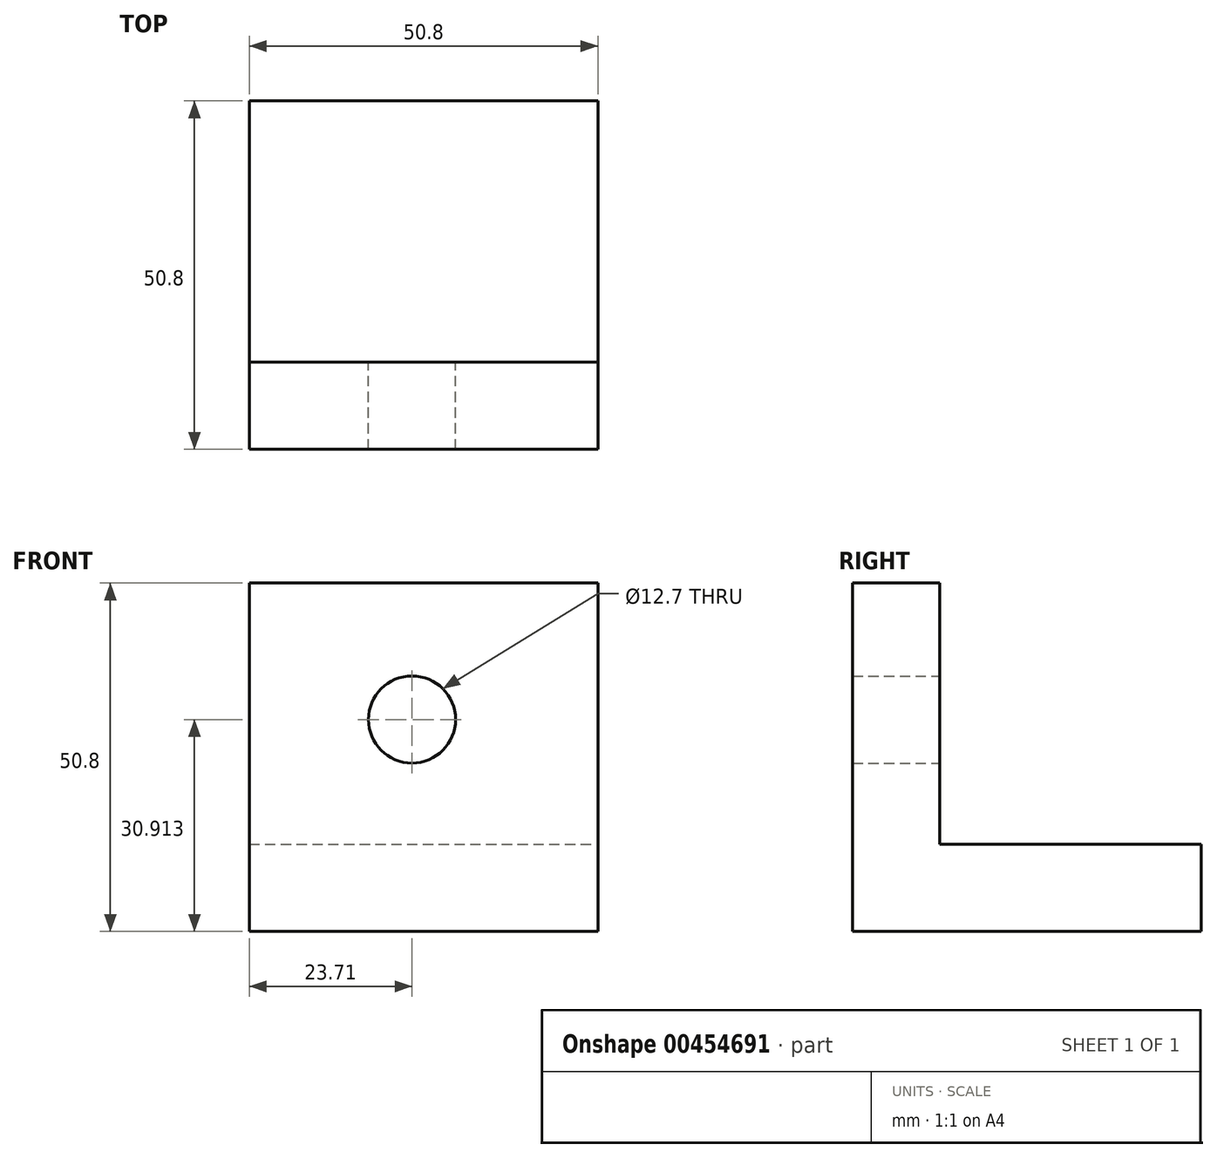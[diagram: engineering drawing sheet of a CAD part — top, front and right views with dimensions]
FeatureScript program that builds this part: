
annotation { "Feature Type Name" : "Feature", "Feature Type Description" : "" }
export const myFeature = defineFeature(function(context is Context, id is Id, definition is map)
    precondition{}
    {
        {
            var Q0;
            Q0=qCreatedBy(makeId("Top.planeOp"),FACE);
            var sketch = newSketch(context, id + "F0", { "sketchPlane" : qUnion([Q0])});
            skLineSegment(sketch, "E0.bottom", {"start": v(-23.71, 28.97) * mm, "end": v(27.09, 28.97) * mm});
            skLineSegment(sketch, "E0.top", {"start": v(-23.71, -21.83) * mm, "end": v(27.09, -21.83) * mm});
            skLineSegment(sketch, "E0.left", {"start": v(-23.71, 28.97) * mm, "end": v(-23.71, -21.83) * mm});
            skLineSegment(sketch, "E0.right", {"start": v(27.09, 28.97) * mm, "end": v(27.09, -21.83) * mm});
            skSolve(sketch);
        }
        {
            var Q0;
            Q0 = qSketchRegion(id + "F0", true);
            extrude(context, id + "F1", {"entities" : qUnion([Q0]), "depth" : 12.7 * mm});
        }
        {
            var Q0;
            Q0=makeQuery(id+"F1.opExtrude","SWEPT_FACE",FACE,{"disambiguationData":[OSD([sQuery(id+"F0.wireOp",EDGE,"E0.top")])]});
            var sketch = newSketch(context, id + "F2", { "sketchPlane" : qUnion([Q0])});
            skLineSegment(sketch, "E1.bottom", {"start": v(-23.71, 0) * mm, "end": v(27.09, 0) * mm});
            skLineSegment(sketch, "E1.top", {"start": v(-23.71, 50.8) * mm, "end": v(27.09, 50.8) * mm});
            skLineSegment(sketch, "E1.left", {"start": v(-23.71, 0) * mm, "end": v(-23.71, 50.8) * mm});
            skLineSegment(sketch, "E1.right", {"start": v(27.09, 0) * mm, "end": v(27.09, 50.8) * mm});
            skSolve(sketch);
        }
        {
            var Q0;
            Q0 = qSketchRegion(id + "F2", true);
            extrude(context, id + "F3", {"entities" : qUnion([Q0]), "operationType" : NewBodyOperationType.ADD, "oppositeDirection" : true, "depth" : 12.7 * mm});
        }
        {
            var Q0;
            Q0=makeQuery(id+"F3.opExtrude","CAP_FACE",FACE,{"disambiguationData":[OSD([sQuery(id+"F2.wireOp",EDGE,"E1.bottom"),sQuery(id+"F2.wireOp",EDGE,"E1.top"),sQuery(id+"F2.wireOp",EDGE,"E1.left"),sQuery(id+"F2.wireOp",EDGE,"E1.right")])],"isStart":false});
            var sketch = newSketch(context, id + "F4", { "sketchPlane" : qUnion([Q0])});
            skCircle(sketch, "E2", {"center": v(0, 30.91) * mm, "radius": 6.35 * mm});
            skSolve(sketch);
        }
        {
            var Q0;
            Q0 = qSketchRegion(id + "F4", true);
            extrude(context, id + "F5", {"entities" : qUnion([Q0]), "operationType" : NewBodyOperationType.REMOVE, "oppositeDirection" : true, "depth" : 15.24 * mm});
        }
    });
